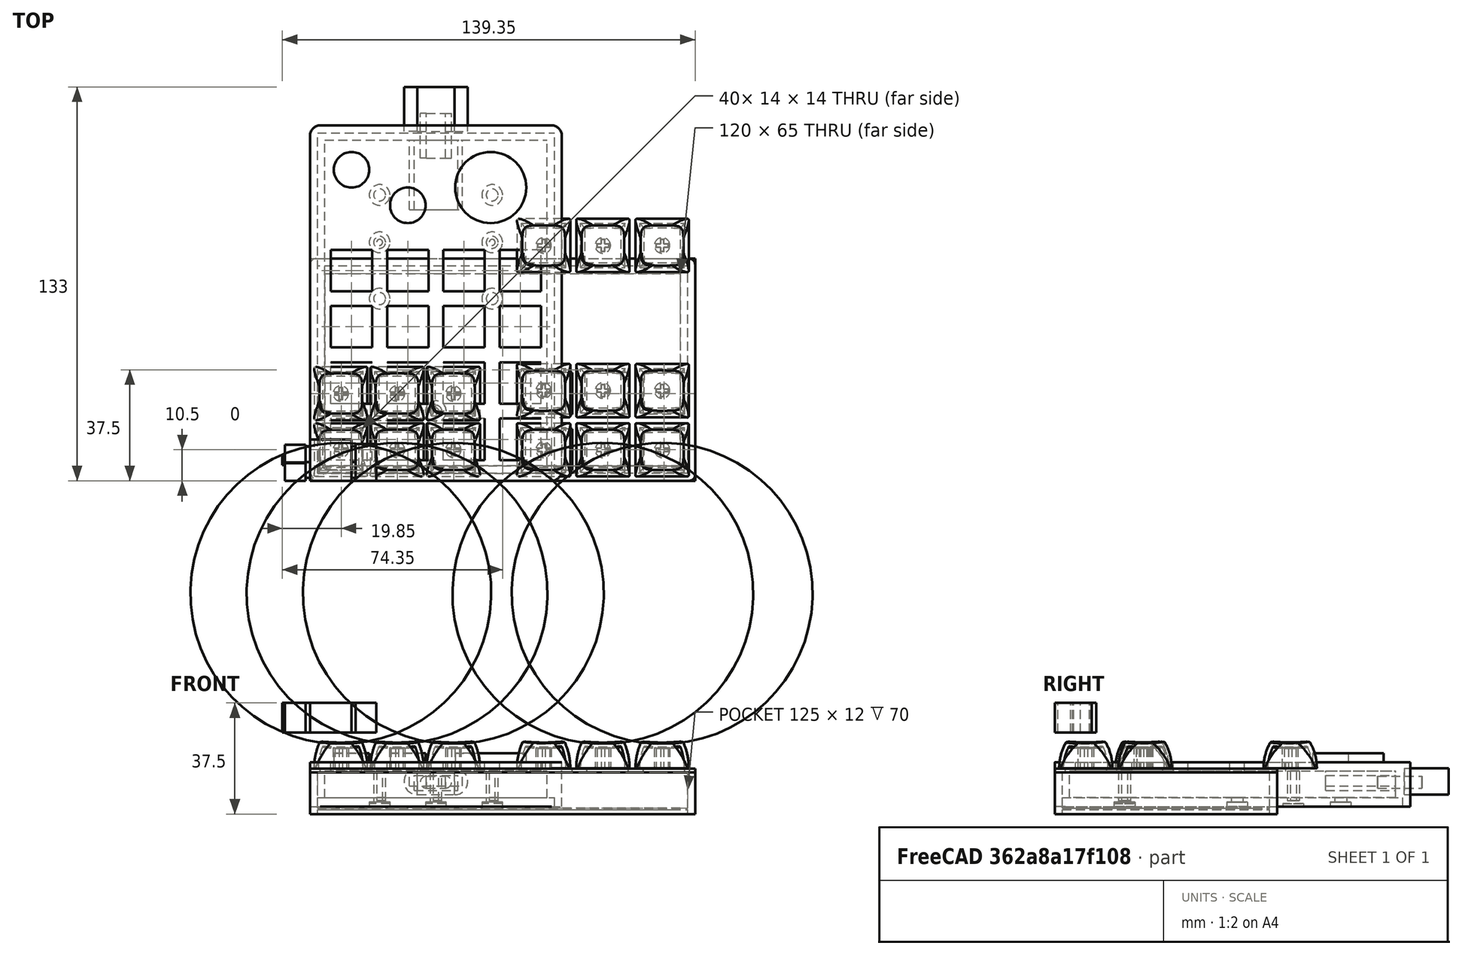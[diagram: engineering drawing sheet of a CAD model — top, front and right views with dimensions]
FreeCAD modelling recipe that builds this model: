
FCSTD DOCUMENT  (FreeCAD 1.0R39109 (Git))
Label: control-v0.6-b
License: All rights reserved
LicenseURL: https://en.wikipedia.org/wiki/All_rights_reserved
objects: Part::Box×51, Part::Cut×43, Part::Cylinder×26, Part::Feature×15, App::DocumentObjectGroup×7, Part::Fillet×3, Part::FeaturePython×1
note: 139 computed .brp shape members not serialized (recipe doc carries the construction recipe); baked Part::Feature solids carry a one-line shape summary decoded from their .brp

FEATURE [Part::Box] Box  label="Upper Housing"
  AttacherType = Attacher::AttachEngine3D
  Height = 1.35
  Length = 130
  Placement = pos=(0,0,11.5) rot=(0,0,1;0rad)
  Width = 75
FEATURE [Part::Box] Box001  label="Cube"
  AttacherType = Attacher::AttachEngine3D
  Height = 4
  Length = 14
  Placement = pos=(3.5,3.5,10) rot=(0,0,1;0rad)
  Width = 14
FEATURE [Part::Box] Box002  label="Cube001"
  AttacherType = Attacher::AttachEngine3D
  Height = 4
  Length = 14
  Placement = pos=(3.5,22.5,10) rot=(0,0,1;0rad)
  Width = 14
FEATURE [Part::Box] Box003  label="Cube002"
  AttacherType = Attacher::AttachEngine3D
  Height = 4
  Length = 14
  Placement = pos=(22.5,22.5,10) rot=(0,0,1;0rad)
  Width = 14
FEATURE [Part::Box] Box005  label="Cube004"
  AttacherType = Attacher::AttachEngine3D
  Height = 4
  Length = 14
  Placement = pos=(41.5,3.5,10) rot=(0,0,1;0rad)
  Width = 14
FEATURE [Part::Box] Box006  label="Cube005"
  AttacherType = Attacher::AttachEngine3D
  Height = 4
  Length = 14
  Placement = pos=(41.5,22.5,10) rot=(0,0,1;0rad)
  Width = 14
FEATURE [Part::Box] Box007  label="Cube006"
  AttacherType = Attacher::AttachEngine3D
  Height = 4
  Length = 14
  Placement = pos=(112.5,3.5,10) rot=(0,0,1;0rad)
  Width = 14
FEATURE [Part::Box] Box008  label="Cube007"
  AttacherType = Attacher::AttachEngine3D
  Height = 4
  Length = 14
  Placement = pos=(93.5,3.5,10) rot=(0,0,1;0rad)
  Width = 14
FEATURE [Part::Box] Box009  label="Cube008"
  AttacherType = Attacher::AttachEngine3D
  Height = 4
  Length = 14
  Placement = pos=(74.5,3.5,10) rot=(0,0,1;0rad)
  Width = 14
FEATURE [Part::Box] Box010  label="Cube009"
  AttacherType = Attacher::AttachEngine3D
  Height = 4
  Length = 14
  Placement = pos=(74.5,22.5,10) rot=(0,0,1;0rad)
  Width = 14
FEATURE [Part::Box] Box011  label="Cube010"
  AttacherType = Attacher::AttachEngine3D
  Height = 4
  Length = 14
  Placement = pos=(93.5,22.5,10) rot=(0,0,1;0rad)
  Width = 14
FEATURE [Part::Box] Box012  label="Cube011"
  AttacherType = Attacher::AttachEngine3D
  Height = 4
  Length = 14
  Placement = pos=(112.5,22.5,10) rot=(0,0,1;0rad)
  Width = 14
FEATURE [Part::Cylinder] Cylinder
  Angle = 360
  AttacherType = Attacher::AttachEngine3D
  FirstAngle = 0
  Height = 3
  Placement = pos=(14,105,15) rot=(0,0,1;0rad)
  Radius = 6
  SecondAngle = 0
FEATURE [Part::Cylinder] Cylinder001
  Angle = 360
  AttacherType = Attacher::AttachEngine3D
  FirstAngle = 0
  Height = 3
  Placement = pos=(33,93,15) rot=(0,0,1;0rad)
  Radius = 6
  SecondAngle = 0
FEATURE [Part::Feature] Part__Feature  label="1u v2"
  Placement = pos=(21.5,15,13) rot=(1,0,0;1.5708rad)
  shape: bbox 18 x 18.01 x 11.79 mm, 51 faces (baked)
FEATURE [Part::Box] Box004  label="Cube003"
  AttacherType = Attacher::AttachEngine3D
  Height = 4
  Length = 14
  Placement = pos=(22.5,3.5,10) rot=(0,0,1;0rad)
  Width = 14
FEATURE [Part::Feature] Part__Feature001  label="1u v003"
  Placement = pos=(40.5,15,13) rot=(1,0,0;1.5708rad)
  shape: bbox 18 x 18.01 x 11.79 mm, 51 faces (baked)
FEATURE [Part::Feature] Part__Feature002  label="1u v004"
  Placement = pos=(59.5,15,13) rot=(1,0,0;1.5708rad)
  shape: bbox 18 x 18.01 x 11.79 mm, 51 faces (baked)
FEATURE [Part::Feature] Part__Feature003  label="1u v005"
  Placement = pos=(59.5,34,13) rot=(1,0,0;1.5708rad)
  shape: bbox 18 x 18.01 x 11.79 mm, 51 faces (baked)
FEATURE [Part::Feature] Part__Feature004  label="1u v006"
  Placement = pos=(21.5,34,13) rot=(1,0,0;1.5708rad)
  shape: bbox 18 x 18.01 x 11.79 mm, 51 faces (baked)
FEATURE [Part::Feature] Part__Feature005  label="1u v007"
  Placement = pos=(40.5,34,13) rot=(1,0,0;1.5708rad)
  shape: bbox 18 x 18.01 x 11.79 mm, 51 faces (baked)
FEATURE [Part::Feature] Part__Feature006  label="1u v008"
  Placement = pos=(90,35,13) rot=(1,0,0;1.5708rad)
  shape: bbox 18 x 18.01 x 11.79 mm, 51 faces (baked)
FEATURE [Part::Feature] Part__Feature007  label="1u v009"
  Placement = pos=(90,15,13) rot=(1,0,0;1.5708rad)
  shape: bbox 18 x 18.01 x 11.79 mm, 51 faces (baked)
FEATURE [Part::Feature] Part__Feature008  label="1u v010"
  Placement = pos=(110,15,13) rot=(1,0,0;1.5708rad)
  shape: bbox 18 x 18.01 x 11.79 mm, 51 faces (baked)
FEATURE [Part::Feature] Part__Feature009  label="1u v011"
  Placement = pos=(110,35,13) rot=(1,0,0;1.5708rad)
  shape: bbox 18 x 18.01 x 11.79 mm, 51 faces (baked)
FEATURE [Part::Feature] Part__Feature010  label="1u v012"
  Placement = pos=(130,15,13) rot=(1,0,0;1.5708rad)
  shape: bbox 18 x 18.01 x 11.79 mm, 51 faces (baked)
FEATURE [Part::Feature] Part__Feature011  label="1u v013"
  Placement = pos=(130,35,13) rot=(1,0,0;1.5708rad)
  shape: bbox 18 x 18.01 x 11.79 mm, 51 faces (baked)
FEATURE [Part::Feature] Part__Feature012  label="1u v014"
  Placement = pos=(130,84,13) rot=(1,0,0;1.5708rad)
  shape: bbox 18 x 18.01 x 11.79 mm, 51 faces (baked)
FEATURE [Part::Feature] Part__Feature013  label="1u v015"
  Placement = pos=(110,84,13) rot=(1,0,0;1.5708rad)
  shape: bbox 18 x 18.01 x 11.79 mm, 51 faces (baked)
FEATURE [Part::Feature] Part__Feature014  label="1u v016"
  Placement = pos=(90,84,13) rot=(1,0,0;1.5708rad)
  shape: bbox 18 x 18.01 x 11.79 mm, 51 faces (baked)
FEATURE [App::DocumentObjectGroup] Group004  label="Keycaps"
  Group = -> [Part__Feature,Part__Feature001,Part__Feature002,Part__Feature004,Part__Feature005,Part__Feature003,Part__Feature007,Part__Feature008,Part__Feature010,Part__Feature006,Part__Feature009,Part__Feature011,Part__Feature012,Part__Feature013,Part__Feature014]
FEATURE [Part::Cut] Cut
  Base = -> Box
  Tool = -> Box001
FEATURE [Part::Cut] Cut001
  Base = -> Cut
  Tool = -> Box004
FEATURE [Part::Cut] Cut002
  Base = -> Cut001
  Tool = -> Box005
FEATURE [Part::Cut] Cut003
  Base = -> Cut002
  Tool = -> Box002
FEATURE [Part::Cut] Cut004
  Base = -> Cut003
  Tool = -> Box003
FEATURE [Part::Cut] Cut005
  Base = -> Cut004
  Tool = -> Box006
FEATURE [Part::Cut] Cut006
  Base = -> Cut005
  Tool = -> Box009
FEATURE [Part::Cut] Cut007
  Base = -> Cut006
  Tool = -> Box008
FEATURE [Part::Cut] Cut008
  Base = -> Cut007
  Tool = -> Box007
FEATURE [Part::Cut] Cut009
  Base = -> Cut008
  Tool = -> Box010
FEATURE [Part::Cut] Cut010
  Base = -> Cut009
  Tool = -> Box011
FEATURE [Part::Cut] Cut011
  Base = -> Cut010
  Tool = -> Box012
FEATURE [App::DocumentObjectGroup] Group001  label="Upper Housing2"
  Group = -> [Cut011]
FEATURE [Part::Box] Box016  label="Cube015"
  AttacherType = Attacher::AttachEngine3D
  Height = 15
  Length = 130
  Placement = pos=(0,0,-13.5) rot=(0,0,1;0rad)
  Width = 75
FEATURE [Part::Box] Box017  label="Cube016"
  AttacherType = Attacher::AttachEngine3D
  Height = 17.5
  Length = 125
  Placement = pos=(2.5,2.5,-11.5) rot=(0,0,1;0rad)
  Width = 70
FEATURE [Part::Cut] Cut012
  Base = -> Box016
  Placement = pos=(0,0,11) rot=(0,0,1;0rad)
  Tool = -> Box017
FEATURE [Part::Box] Box019  label="Cube018"
  AttacherType = Attacher::AttachEngine3D
  Height = 10
  Length = 14
  Placement = pos=(0,0,25) rot=(0,0,1;0rad)
  Width = 14
FEATURE [Part::Box] Box020  label="Cube019"
  AttacherType = Attacher::AttachEngine3D
  Height = 10
  Length = 1.35
  Placement = pos=(14,6.35,25) rot=(0,0,1;0rad)
  Width = 5.35
FEATURE [Part::Box] Box021  label="Cube020"
  AttacherType = Attacher::AttachEngine3D
  Height = 10
  Length = 1.4
  Placement = pos=(14,1,25) rot=(0,0,1;0rad)
  Width = 5.35
FEATURE [Part::Box] Box022  label="Cube021"
  AttacherType = Attacher::AttachEngine3D
  Height = 10
  Length = 1.45
  Placement = pos=(-1.45,6.35,25) rot=(0,0,1;0rad)
  Width = 5.35
FEATURE [Part::Box] Box023  label="Cube022"
  AttacherType = Attacher::AttachEngine3D
  Height = 10
  Length = 1.5
  Placement = pos=(-1.5,1,25) rot=(0,0,1;0rad)
  Width = 5.35
FEATURE [Part::Box] Box024  label="Cube023"
  AttacherType = Attacher::AttachEngine3D
  Height = 10
  Length = 7
  Placement = pos=(-8.45,6,25) rot=(0,0,1;0rad)
  Width = 6.22
FEATURE [Part::Box] Box025  label="Cube024"
  AttacherType = Attacher::AttachEngine3D
  Height = 10
  Length = 0.9
  Placement = pos=(-9.35,5.35,25) rot=(0,0,1;0rad)
  Width = 3.3
FEATURE [Part::Box] Box026  label="Cube025"
  AttacherType = Attacher::AttachEngine3D
  Height = 10
  Length = 7
  Placement = pos=(15.4,0,25) rot=(0,0,1;0rad)
  Width = 12.45
FEATURE [Part::Box] Box027  label="Cube026"
  AttacherType = Attacher::AttachEngine3D
  Height = 10
  Length = 7
  Placement = pos=(-8.5,0,25) rot=(0,0,1;0rad)
  Width = 6.22
FEATURE [App::DocumentObjectGroup] Group  label="Stab"
  Group = -> [Box019,Box022,Box021,Box023,Box024,Box027,Box025,Box026,Box020]
FEATURE [Part::Box] Box028  label="Cube027"
  AttacherType = Attacher::AttachEngine3D
  Height = 10
  Length = 125
  Placement = pos=(2.5,2.5,-11) rot=(0,0,1;0rad)
  Width = 70
FEATURE [Part::Box] Box029  label="Cube028"
  AttacherType = Attacher::AttachEngine3D
  Height = 14
  Length = 120
  Placement = pos=(5,5,-2.5) rot=(0,0,1;0rad)
  Width = 65
FEATURE [Part::Cut] Cut013
  Base = -> Cut012
  Tool = -> Box029
FEATURE [Part::Cut] Cut014
  Base = -> Cut013
  Tool = -> Box028
FEATURE [Part::FeaturePython] Connect  label="Upper Housing003"  # WARN: FeaturePython — macro-defined, semantics opaque (R4)
  Objects = -> [Group001,Cut014]
  Tolerance = 0
FEATURE [Part::Fillet] Fillet
  Base = -> Connect
  EdgeLinks = -> Connect [Edge5,Edge7,Edge13,Edge14,Edge50,Edge52,Edge102,Edge104,Edge141,Edge150,Edge203,Edge204]
  Edges = 12 edges r=2: [Edge5,Edge7,Edge13,Edge14,Edge50,Edge52,Edge102,Edge104,Edge141,Edge150,Edge203,Edge204]
FEATURE [Part::Box] Box031  label="Cube029"
  AttacherType = Attacher::AttachEngine3D
  Height = 15
  Length = 85
  Width = 120
FEATURE [Part::Box] Box032  label="Cube030"
  AttacherType = Attacher::AttachEngine3D
  Height = 10
  Length = 14
  Placement = pos=(7,7,6) rot=(0,0,1;0rad)
  Width = 14
FEATURE [Part::Box] Box033  label="Cube031"
  AttacherType = Attacher::AttachEngine3D
  Height = 10
  Length = 14
  Placement = pos=(26,7,6) rot=(0,0,1;0rad)
  Width = 14
FEATURE [Part::Box] Box034  label="Cube032"
  AttacherType = Attacher::AttachEngine3D
  Height = 10
  Length = 14
  Placement = pos=(45,7,6) rot=(0,0,1;0rad)
  Width = 14
FEATURE [Part::Box] Box035  label="Cube033"
  AttacherType = Attacher::AttachEngine3D
  Height = 10
  Length = 14
  Placement = pos=(64,7,6) rot=(0,0,1;0rad)
  Width = 14
FEATURE [Part::Box] Box036  label="Cube034"
  AttacherType = Attacher::AttachEngine3D
  Height = 10
  Length = 14
  Placement = pos=(7,26,6) rot=(0,0,1;0rad)
  Width = 14
FEATURE [Part::Box] Box037  label="Cube035"
  AttacherType = Attacher::AttachEngine3D
  Height = 10
  Length = 14
  Placement = pos=(26,26,6) rot=(0,0,1;0rad)
  Width = 14
FEATURE [Part::Box] Box038  label="Cube036"
  AttacherType = Attacher::AttachEngine3D
  Height = 10
  Length = 14
  Placement = pos=(45,26,6) rot=(0,0,1;0rad)
  Width = 14
FEATURE [Part::Box] Box039  label="Cube037"
  AttacherType = Attacher::AttachEngine3D
  Height = 10
  Length = 14
  Placement = pos=(64,26,6) rot=(0,0,1;0rad)
  Width = 14
FEATURE [Part::Box] Box040  label="Cube038"
  AttacherType = Attacher::AttachEngine3D
  Height = 10
  Length = 14
  Placement = pos=(7,45,6) rot=(0,0,1;0rad)
  Width = 14
FEATURE [Part::Box] Box041  label="Cube039"
  AttacherType = Attacher::AttachEngine3D
  Height = 10
  Length = 14
  Placement = pos=(26,45,6) rot=(0,0,1;0rad)
  Width = 14
FEATURE [Part::Box] Box042  label="Cube040"
  AttacherType = Attacher::AttachEngine3D
  Height = 10
  Length = 14
  Placement = pos=(45,45,6) rot=(0,0,1;0rad)
  Width = 14
FEATURE [Part::Box] Box043  label="Cube041"
  AttacherType = Attacher::AttachEngine3D
  Height = 10
  Length = 14
  Placement = pos=(64,45,6) rot=(0,0,1;0rad)
  Width = 14
FEATURE [Part::Cylinder] Cylinder002
  Angle = 360
  AttacherType = Attacher::AttachEngine3D
  FirstAngle = 0
  Height = 3
  Placement = pos=(61,99,15) rot=(0,0,1;0rad)
  Radius = 12
  SecondAngle = 0
FEATURE [App::DocumentObjectGroup] Group003  label="Rotories"
  Group = -> [Cylinder,Cylinder001,Cylinder002]
FEATURE [Part::Box] Box044  label="Cube042"
  AttacherType = Attacher::AttachEngine3D
  Height = 10
  Length = 14
  Placement = pos=(7,64,6) rot=(0,0,1;0rad)
  Width = 14
FEATURE [Part::Box] Box045  label="Cube043"
  AttacherType = Attacher::AttachEngine3D
  Height = 10
  Length = 14
  Placement = pos=(26,64,6) rot=(0,0,1;0rad)
  Width = 14
FEATURE [Part::Box] Box046  label="Cube044"
  AttacherType = Attacher::AttachEngine3D
  Height = 10
  Length = 14
  Placement = pos=(45,64,6) rot=(0,0,1;0rad)
  Width = 14
FEATURE [Part::Box] Box047  label="Cube045"
  AttacherType = Attacher::AttachEngine3D
  Height = 10
  Length = 14
  Placement = pos=(64,64,6) rot=(0,0,1;0rad)
  Width = 14
FEATURE [Part::Box] Box049  label="Cube047"
  AttacherType = Attacher::AttachEngine3D
  Height = 12
  Length = 75
  Placement = pos=(5,5,0) rot=(0,0,1;0rad)
  Width = 110
FEATURE [Part::Box] Box050  label="Lower Housing"
  AttacherType = Attacher::AttachEngine3D
  Height = 3
  Length = 80
  Placement = pos=(2.5,2.5,0) rot=(0,0,1;0rad)
  Width = 115
FEATURE [Part::Box] Box051  label="Cube049"
  AttacherType = Attacher::AttachEngine3D
  Height = 3
  Length = 80
  Placement = pos=(2.5,2.5,0) rot=(0,0,1;0rad)
  Width = 115
FEATURE [Part::Cut] Cut015
  Base = -> Box031
  Tool = -> Box049
FEATURE [Part::Cut] Cut016
  Base = -> Cut015
  Tool = -> Box051
FEATURE [Part::Cut] Cut017
  Base = -> Cut016
  Tool = -> Box032
FEATURE [Part::Cut] Cut018
  Base = -> Cut017
  Tool = -> Box033
FEATURE [Part::Cut] Cut019
  Base = -> Cut018
  Tool = -> Box034
FEATURE [Part::Cut] Cut020
  Base = -> Cut019
  Tool = -> Box035
FEATURE [Part::Cut] Cut021
  Base = -> Cut020
  Tool = -> Box036
FEATURE [Part::Cut] Cut022
  Base = -> Cut021
  Tool = -> Box037
FEATURE [Part::Cut] Cut023
  Base = -> Cut022
  Tool = -> Box038
FEATURE [Part::Cut] Cut024
  Base = -> Cut023
  Tool = -> Box039
FEATURE [Part::Cut] Cut025
  Base = -> Cut024
  Tool = -> Box040
FEATURE [Part::Cut] Cut026
  Base = -> Cut025
  Tool = -> Box041
FEATURE [Part::Cut] Cut027
  Base = -> Cut026
  Tool = -> Box042
FEATURE [Part::Cut] Cut028
  Base = -> Cut027
  Tool = -> Box043
FEATURE [Part::Cut] Cut029
  Base = -> Cut028
  Tool = -> Box044
FEATURE [Part::Cut] Cut030
  Base = -> Cut029
  Tool = -> Box045
FEATURE [Part::Cut] Cut031
  Base = -> Cut030
  Tool = -> Box046
FEATURE [Part::Cut] Cut032
  Base = -> Cut031
  Tool = -> Box047
FEATURE [App::DocumentObjectGroup] Group005  label="Switch Slots"
  Group = -> [Cut032]
FEATURE [Part::Fillet] Fillet001
  Base = -> Cut032
  EdgeLinks = -> Cut032 [Edge1]
  Edges = 1 edges r=3.5: [Edge1]
FEATURE [Part::Fillet] Fillet002
  Base = -> Fillet001
  EdgeLinks = -> Fillet001 [Edge3,Edge76,Edge83]
  Edges = 3 edges r=3.5: [Edge3,Edge76,Edge83]
FEATURE [Part::Cylinder] Cylinder004
  Angle = 360
  AttacherType = Attacher::AttachEngine3D
  FirstAngle = 0
  Height = 10
  Placement = pos=(42.5,23.5,2) rot=(0,0,1;0rad)
  Radius = 2
  SecondAngle = 0
FEATURE [Part::Cylinder] Cylinder005
  Angle = 360
  AttacherType = Attacher::AttachEngine3D
  FirstAngle = 0
  Height = 10
  Placement = pos=(61.5,80.5,2) rot=(0,0,1;0rad)
  Radius = 2
  SecondAngle = 0
FEATURE [Part::Cylinder] Cylinder006
  Angle = 360
  AttacherType = Attacher::AttachEngine3D
  FirstAngle = 0
  Height = 10
  Placement = pos=(23.5,80.5,2) rot=(0,0,1;0rad)
  Radius = 2
  SecondAngle = 0
FEATURE [App::DocumentObjectGroup] Group006  label="Screw Posts"
  Group = -> [Cylinder004,Cylinder005,Cylinder006]
FEATURE [Part::Cylinder] Cylinder009
  Angle = 360
  AttacherType = Attacher::AttachEngine3D
  FirstAngle = 0
  Height = 15
  Placement = pos=(42.5,23.5,-13.5) rot=(0,0,1;0rad)
  Radius = 3.5
  SecondAngle = 0
FEATURE [Part::Cylinder] Cylinder010
  Angle = 360
  AttacherType = Attacher::AttachEngine3D
  FirstAngle = 0
  Height = 15
  Placement = pos=(61.5,61.5,-13.5) rot=(0,0,1;0rad)
  Radius = 3.5
  SecondAngle = 0
FEATURE [Part::Cylinder] Cylinder011
  Angle = 360
  AttacherType = Attacher::AttachEngine3D
  FirstAngle = 0
  Height = 15
  Placement = pos=(23.5,61.5,-13.5) rot=(0,0,1;0rad)
  Radius = 3.5
  SecondAngle = 0
FEATURE [Part::Cylinder] Cylinder012
  Angle = 360
  AttacherType = Attacher::AttachEngine3D
  FirstAngle = 0
  Height = 15
  Placement = pos=(61.5,96.5,-13.5) rot=(0,0,1;0rad)
  Radius = 3.5
  SecondAngle = 0
FEATURE [Part::Cylinder] Cylinder013
  Angle = 360
  AttacherType = Attacher::AttachEngine3D
  FirstAngle = 0
  Height = 15
  Placement = pos=(23.5,96.5,-13.5) rot=(0,0,1;0rad)
  Radius = 3.5
  SecondAngle = 0
FEATURE [Part::Cut] Cut033
  Base = -> Box050
  Tool = -> Cylinder009
FEATURE [Part::Cut] Cut034
  Base = -> Cut033
  Tool = -> Cylinder010
FEATURE [Part::Cut] Cut035
  Base = -> Cut034
  Tool = -> Cylinder011
FEATURE [Part::Cut] Cut036
  Base = -> Cut035
  Tool = -> Cylinder012
FEATURE [Part::Cut] Cut037
  Base = -> Cut036
  Tool = -> Cylinder013
FEATURE [Part::Cylinder] Cylinder014
  Angle = 360
  AttacherType = Attacher::AttachEngine3D
  FirstAngle = 0
  Height = 15
  Placement = pos=(42.5,23.5,-3) rot=(0,0,1;0rad)
  Radius = 2
  SecondAngle = 0
FEATURE [Part::Cylinder] Cylinder015
  Angle = 360
  AttacherType = Attacher::AttachEngine3D
  FirstAngle = 0
  Height = 15
  Placement = pos=(61.5,61.5,-3) rot=(0,0,1;0rad)
  Radius = 2
  SecondAngle = 0
FEATURE [Part::Cylinder] Cylinder016
  Angle = 360
  AttacherType = Attacher::AttachEngine3D
  FirstAngle = 0
  Height = 15
  Placement = pos=(23.5,61.5,-3) rot=(0,0,1;0rad)
  Radius = 2
  SecondAngle = 0
FEATURE [Part::Cylinder] Cylinder017
  Angle = 360
  AttacherType = Attacher::AttachEngine3D
  FirstAngle = 0
  Height = 15
  Placement = pos=(61.5,96.5,-3) rot=(0,0,1;0rad)
  Radius = 2
  SecondAngle = 0
FEATURE [Part::Cylinder] Cylinder018
  Angle = 360
  AttacherType = Attacher::AttachEngine3D
  FirstAngle = 0
  Height = 15
  Placement = pos=(23.5,96.5,-3) rot=(0,0,1;0rad)
  Radius = 2
  SecondAngle = 0
FEATURE [Part::Cut] Cut038
  Base = -> Cut037
  Tool = -> Cylinder014
FEATURE [Part::Cut] Cut039
  Base = -> Cut038
  Tool = -> Cylinder015
FEATURE [Part::Cut] Cut040
  Base = -> Cut039
  Tool = -> Cylinder016
FEATURE [Part::Cut] Cut041
  Base = -> Cut040
  Tool = -> Cylinder017
FEATURE [Part::Cut] Cut042
  Base = -> Cut041
  Tool = -> Cylinder018
FEATURE [Part::Cylinder] Cylinder019
  Angle = 360
  AttacherType = Attacher::AttachEngine3D
  FirstAngle = 0
  Height = 10
  Placement = pos=(42.5,23.5,2) rot=(0,0,1;0rad)
  Radius = 1
  SecondAngle = 0
FEATURE [Part::Cylinder] Cylinder020
  Angle = 360
  AttacherType = Attacher::AttachEngine3D
  FirstAngle = 0
  Height = 1
  Placement = pos=(42.5,23.5,0) rot=(0,0,1;0rad)
  Radius = 3.5
  SecondAngle = 0
FEATURE [Part::Cylinder] Cylinder021
  Angle = 360
  AttacherType = Attacher::AttachEngine3D
  FirstAngle = 0
  Height = 10
  Placement = pos=(61.5,80.5,2) rot=(0,0,1;0rad)
  Radius = 1
  SecondAngle = 0
FEATURE [Part::Cylinder] Cylinder022
  Angle = 360
  AttacherType = Attacher::AttachEngine3D
  FirstAngle = 0
  Height = 1
  Placement = pos=(61.5,80.5,0) rot=(0,0,1;0rad)
  Radius = 3.5
  SecondAngle = 0
FEATURE [Part::Cylinder] Cylinder023
  Angle = 360
  AttacherType = Attacher::AttachEngine3D
  FirstAngle = 0
  Height = 10
  Placement = pos=(23.5,80.5,2) rot=(0,0,1;0rad)
  Radius = 1
  SecondAngle = 0
FEATURE [Part::Cylinder] Cylinder024
  Angle = 360
  AttacherType = Attacher::AttachEngine3D
  FirstAngle = 0
  Height = 1
  Placement = pos=(23.5,80.5,0) rot=(0,0,1;0rad)
  Radius = 3.5
  SecondAngle = 0
FEATURE [App::DocumentObjectGroup] Group007  label=""Screws""
  Group = -> [Cylinder019,Cylinder020,Cylinder021,Cylinder022,Cylinder023,Cylinder024]
FEATURE [Part::Box] Box052  label="Cube050"
  AttacherType = Attacher::AttachEngine3D
  Height = 3
  Length = 80
  Placement = pos=(2.5,2.5,0) rot=(0,0,1;0rad)
  Width = 115
FEATURE [Part::Box] Box053  label="rp2040-zero"
  AttacherType = Attacher::AttachEngine3D
  Height = 5
  Length = 18
  Placement = pos=(33.5,91.5,7) rot=(0,0,1;0rad)
  Width = 23.5
FEATURE [Part::Box] Box054  label="rp2040-zero001"
  AttacherType = Attacher::AttachEngine3D
  Height = 5
  Length = 14.62
  Placement = pos=(35.25,91.5,5.5) rot=(0,0,1;0rad)
  Width = 23.5
FEATURE [Part::Box] Box056  label="Cube052"
  AttacherType = Attacher::AttachEngine3D
  Height = 4
  Length = 6.5
  Placement = pos=(39.25,109,6.25) rot=(0,0,1;0rad)
  Width = 15
FEATURE [Part::Cylinder] Cylinder025
  Angle = 180
  AttacherType = Attacher::AttachEngine3D
  FirstAngle = 0
  Height = 15
  Placement = pos=(39.25,124,8.25) rot=(-0.58,0.58,-0.58;4.18879rad)
  Radius = 2
  SecondAngle = 0
FEATURE [Part::Cylinder] Cylinder026
  Angle = 180
  AttacherType = Attacher::AttachEngine3D
  FirstAngle = 0
  Height = 15
  Placement = pos=(45.75,124,8.25) rot=(-0.58,-0.58,0.58;4.18879rad)
  Radius = 2
  SecondAngle = 0
FEATURE [Part::Box] Box057  label="Cube053"
  AttacherType = Attacher::AttachEngine3D
  Height = 9
  Length = 12.5
  Placement = pos=(36.25,118,4) rot=(0,0,1;0rad)
  Width = 15
FEATURE [Part::Cylinder] Cylinder027
  Angle = 180
  AttacherType = Attacher::AttachEngine3D
  FirstAngle = 0
  Height = 15
  Placement = pos=(36.25,133,8.5) rot=(-0.58,0.58,-0.58;4.18879rad)
  Radius = 4.5
  SecondAngle = 0
FEATURE [Part::Cylinder] Cylinder028
  Angle = 180
  AttacherType = Attacher::AttachEngine3D
  FirstAngle = 0
  Height = 15
  Placement = pos=(48.75,133,8.5) rot=(-0.58,-0.58,0.58;4.18879rad)
  Radius = 4.5
  SecondAngle = 0
